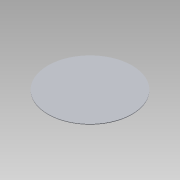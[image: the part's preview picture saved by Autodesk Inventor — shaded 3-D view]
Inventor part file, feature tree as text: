
AUTODESK INVENTOR PART (.ipt)
format: ipt  version: 2015 SP1 (Build 190203100, 203)  size: 73,728 bytes
history: native  units: mm
features: extrude x1, sketch x1
ambient origin geometry x8: Origin, YZ Plane, XZ Plane, XY Plane, X Axis, Y Axis, Z Axis, Center Point
bodies: Solid1 (feature_tree)
feature tree (2):
  extrude  "Extrusion1"  Depth=4.0mm TaperAngle=0.0deg
  sketch  "Sketch1"  dims[d0=600.0mm d1=4.0mm d2=0.0mm]
